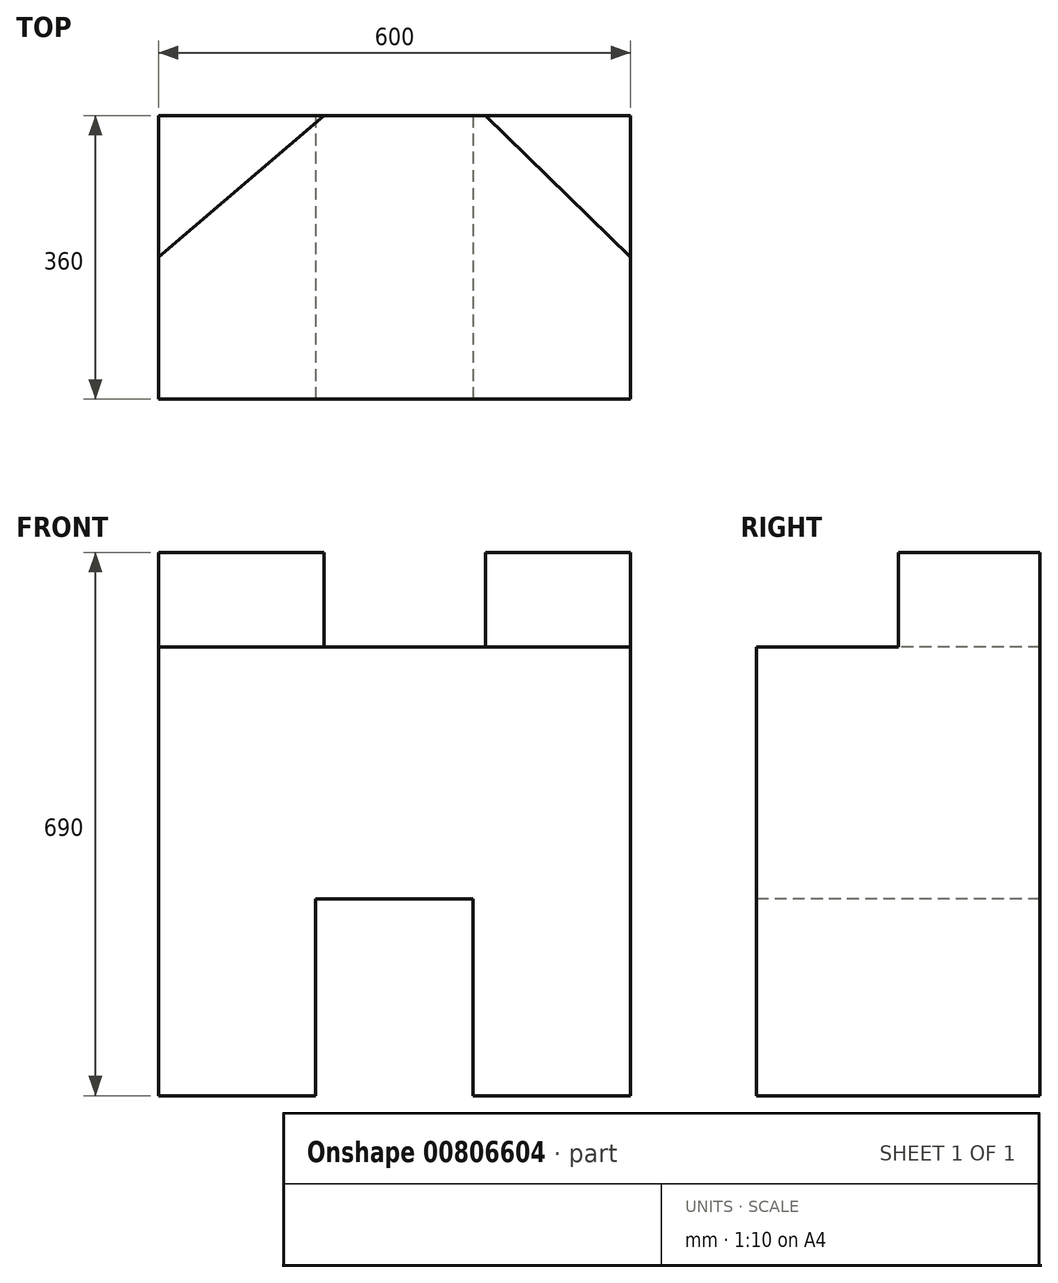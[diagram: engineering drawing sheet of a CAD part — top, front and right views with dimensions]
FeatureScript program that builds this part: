
annotation { "Feature Type Name" : "Feature", "Feature Type Description" : "" }
export const myFeature = defineFeature(function(context is Context, id is Id, definition is map)
    precondition{}
    {
        {
            var Q0;
            Q0=qCreatedBy(makeId("Front.planeOp"),FACE);
            var sketch = newSketch(context, id + "F0", { "sketchPlane" : qUnion([Q0])});
            skLineSegment(sketch, "E0.bottom", {"start": v(300, -285) * mm, "end": v(-300, -285) * mm});
            skLineSegment(sketch, "E0.top", {"start": v(300, 285) * mm, "end": v(-300, 285) * mm});
            skLineSegment(sketch, "E0.left", {"start": v(300, -285) * mm, "end": v(300, 285) * mm});
            skLineSegment(sketch, "E0.right", {"start": v(-300, -285) * mm, "end": v(-300, 285) * mm});
            skPoint(sketch, "E0.middle", {"position": v(0, 0) * mm});
            skSolve(sketch);
        }
        {
            var Q0;
            Q0=makeQuery(id+"F0.imprint","IMPRINT",FACE,{"disambiguationData":[TD([[makeQuery(id+"F0.imprint","IMPRINT",EDGE,{"derivedFrom":sQuery(id+"F0.wireOp",EDGE,"E0.bottom")}),-1.0]])]});
            extrude(context, id + "F1", {"entities" : qUnion([Q0]), "depth" : 360 * mm, "offsetDistance" : 25 * mm});
        }
        {
            var Q0;
            Q0=makeQuery(id+"F1.opExtrude","CAP_FACE",FACE,{"disambiguationData":[OSD([sQuery(id+"F0.wireOp",EDGE,"E0.bottom"),sQuery(id+"F0.wireOp",EDGE,"E0.top"),sQuery(id+"F0.wireOp",EDGE,"E0.left"),sQuery(id+"F0.wireOp",EDGE,"E0.right")])],"isStart":false});
            var sketch = newSketch(context, id + "F2", { "sketchPlane" : qUnion([Q0])});
            skLineSegment(sketch, "E1.bottom", {"start": v(-100, -285) * mm, "end": v(100, -285) * mm});
            skLineSegment(sketch, "E1.top", {"start": v(-100, -35) * mm, "end": v(100, -35) * mm});
            skLineSegment(sketch, "E1.left", {"start": v(-100, -285) * mm, "end": v(-100, -35) * mm});
            skLineSegment(sketch, "E1.right", {"start": v(100, -285) * mm, "end": v(100, -35) * mm});
            skPoint(sketch, "E1.middle", {"position": v(0, -160) * mm});
            skSolve(sketch);
        }
        {
            var Q0;
            Q0 = qSketchRegion(id + "F2", true);
            extrude(context, id + "F3", {"entities" : qUnion([Q0]), "operationType" : NewBodyOperationType.REMOVE, "oppositeDirection" : true, "depth" : 500 * mm, "offsetDistance" : 25 * mm});
        }
        {
            var Q0;
            Q0=makeQuery(id+"F1.opExtrude","SWEPT_FACE",FACE,{"disambiguationData":[OSD([sQuery(id+"F0.wireOp",EDGE,"E0.top")])]});
            var sketch = newSketch(context, id + "F4", { "sketchPlane" : qUnion([Q0])});
            skLineSegment(sketch, "E2.bottom", {"start": v(-300, 0) * mm, "end": v(-89.63, 0) * mm});
            skLineSegment(sketch, "E2.top", {"start": v(-300, -180) * mm, "end": v(-89.63, -180) * mm});
            skLineSegment(sketch, "E2.left", {"start": v(-300, 0) * mm, "end": v(-300, -180) * mm});
            skLineSegment(sketch, "E2.right", {"start": v(-89.63, 0) * mm, "end": v(-89.63, -180) * mm});
            skSolve(sketch);
        }
        {
            var Q0;
            Q0 = qSketchRegion(id + "F4", true);
            extrude(context, id + "F5", {"entities" : qUnion([Q0]), "operationType" : NewBodyOperationType.ADD, "depth" : 120 * mm, "offsetDistance" : 25 * mm});
        }
        {
            var Q0;
            Q0=makeQuery(id+"F5.opExtrude","CAP_FACE",FACE,{"disambiguationData":[OSD([sQuery(id+"F4.wireOp",EDGE,"E2.bottom"),sQuery(id+"F4.wireOp",EDGE,"E2.top"),sQuery(id+"F4.wireOp",EDGE,"E2.left"),sQuery(id+"F4.wireOp",EDGE,"E2.right")])],"isStart":false});
            var sketch = newSketch(context, id + "F6", { "sketchPlane" : qUnion([Q0])});
            skLineSegment(sketch, "E3", {"start": v(-89.63, 0) * mm, "end": v(-300, -180) * mm});
            skLineSegment(sketch, "E4", {"start": v(-300, -180) * mm, "end": v(-89.63, -180) * mm});
            skLineSegment(sketch, "E5", {"start": v(-89.63, -180) * mm, "end": v(-89.63, 0) * mm});
            skSolve(sketch);
        }
        {
            var Q0;
            Q0 = qSketchRegion(id + "F6", true);
            extrude(context, id + "F7", {"entities" : qUnion([Q0]), "operationType" : NewBodyOperationType.REMOVE, "oppositeDirection" : true, "depth" : 120 * mm, "offsetDistance" : 25 * mm});
        }
        {
            var Q0;
            Q0=makeQuery(id+"F7.boolean.opBoolean","MERGE",FACE,{"derivedFrom":[makeQuery(id+"F1.opExtrude","SWEPT_FACE",FACE,{"disambiguationData":[OSD([sQuery(id+"F0.wireOp",EDGE,"E0.top")])]}),makeQuery(id+"F7.opExtrude","CAP_FACE",FACE,{"disambiguationData":[OSD([sQuery(id+"F6.wireOp",EDGE,"E3"),sQuery(id+"F6.wireOp",EDGE,"E4"),sQuery(id+"F6.wireOp",EDGE,"E5")])],"isStart":false})]});
            var sketch = newSketch(context, id + "F8", { "sketchPlane" : qUnion([Q0])});
            skLineSegment(sketch, "E6.bottom", {"start": v(300, 0) * mm, "end": v(115.32, 0) * mm});
            skLineSegment(sketch, "E6.top", {"start": v(300, -180) * mm, "end": v(115.32, -180) * mm});
            skLineSegment(sketch, "E6.left", {"start": v(300, 0) * mm, "end": v(300, -180) * mm});
            skLineSegment(sketch, "E6.right", {"start": v(115.32, 0) * mm, "end": v(115.32, -180) * mm});
            skSolve(sketch);
        }
        {
            var Q0;
            Q0 = qSketchRegion(id + "F8", true);
            extrude(context, id + "F9", {"entities" : qUnion([Q0]), "operationType" : NewBodyOperationType.ADD, "depth" : 120 * mm, "offsetDistance" : 25 * mm});
        }
        {
            var Q0;
            Q0=makeQuery(id+"F9.opExtrude","CAP_FACE",FACE,{"disambiguationData":[OSD([sQuery(id+"F8.wireOp",EDGE,"E6.bottom"),sQuery(id+"F8.wireOp",EDGE,"E6.top"),sQuery(id+"F8.wireOp",EDGE,"E6.left"),sQuery(id+"F8.wireOp",EDGE,"E6.right")])],"isStart":false});
            var sketch = newSketch(context, id + "F10", { "sketchPlane" : qUnion([Q0])});
            skLineSegment(sketch, "E7", {"start": v(115.32, 0) * mm, "end": v(300, -180) * mm});
            skLineSegment(sketch, "E8", {"start": v(300, -180) * mm, "end": v(115.32, -180) * mm});
            skLineSegment(sketch, "E9", {"start": v(115.32, -180) * mm, "end": v(115.32, 0) * mm});
            skSolve(sketch);
        }
        {
            var Q0;
            Q0 = qSketchRegion(id + "F10", true);
            extrude(context, id + "F11", {"entities" : qUnion([Q0]), "operationType" : NewBodyOperationType.REMOVE, "oppositeDirection" : true, "depth" : 120 * mm, "offsetDistance" : 25 * mm});
        }
    });
